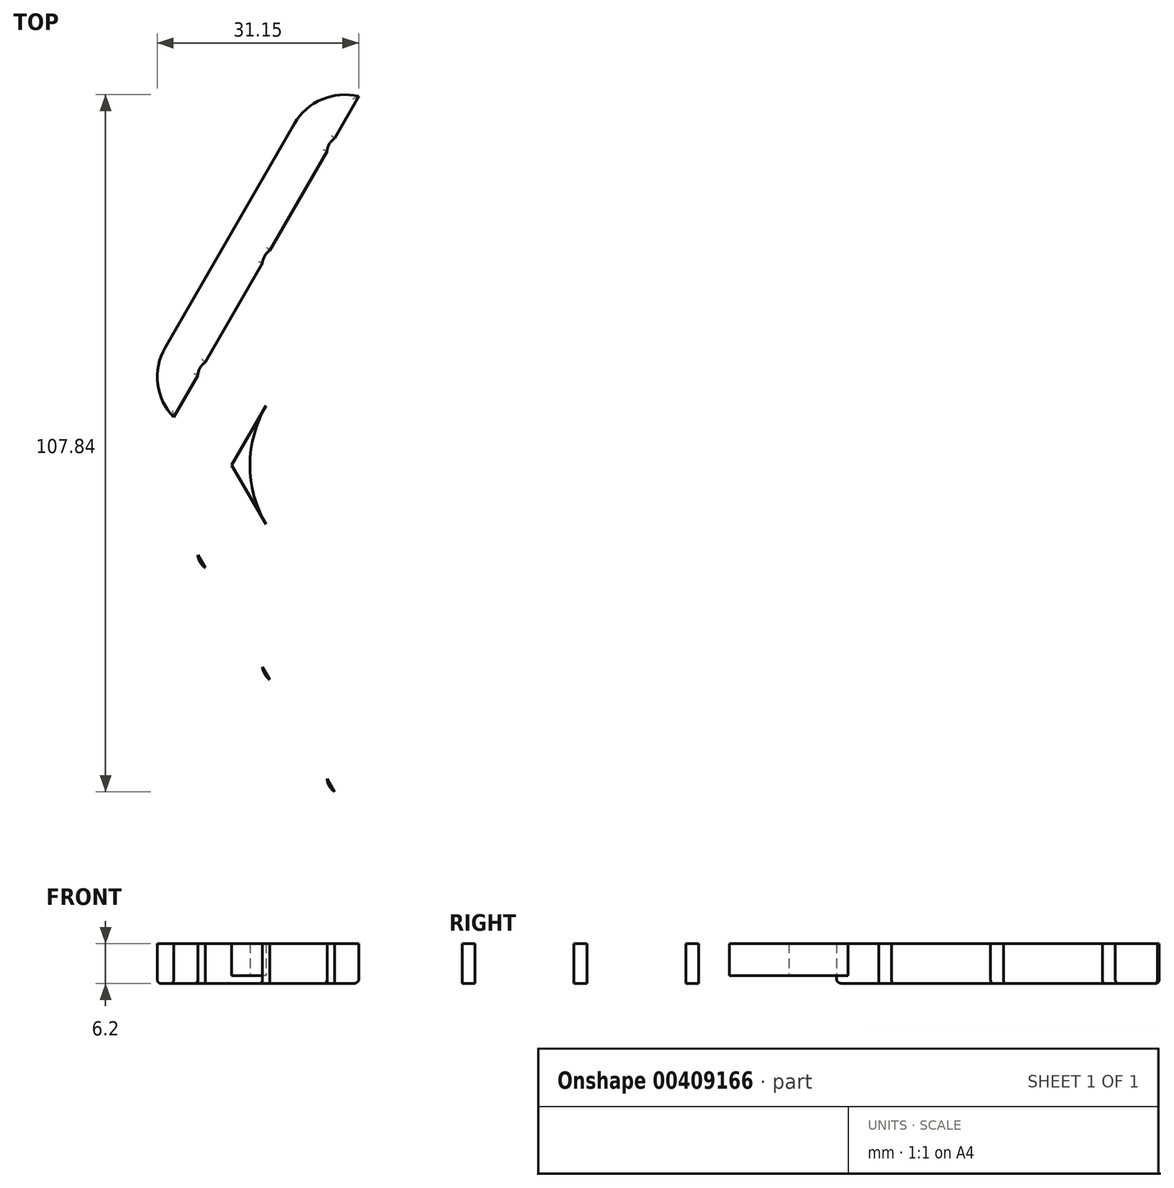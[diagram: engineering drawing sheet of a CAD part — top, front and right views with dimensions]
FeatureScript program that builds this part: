
annotation { "Feature Type Name" : "Feature", "Feature Type Description" : "" }
export const myFeature = defineFeature(function(context is Context, id is Id, definition is map)
    precondition{}
    {
        {
            var Q0;
            Q0=qCreatedBy(makeId("Top.planeOp"),FACE);
            var sketch = newSketch(context, id + "F0", { "sketchPlane" : qUnion([Q0])});
            skLineSegment(sketch, "E0", {"start": v(0, 0) * mm, "end": v(40.15, 69.55) * mm, "construction": true});
            skLineSegment(sketch, "E1", {"start": v(40.15, -69.55) * mm, "end": v(0, 0) * mm, "construction": true});
            skLineSegment(sketch, "E2", {"start": v(-5.77, 10) * mm, "end": v(11.55, 0) * mm, "construction": true});
            skCircle(sketch, "E3", {"center": v(7.89, 13.66) * mm, "radius": 10 * mm, "construction": true});
            skCircle(sketch, "E4", {"center": v(7.89, 13.66) * mm, "radius": 2.75 * mm});
            skCircle(sketch, "E5", {"center": v(17.89, 30.98) * mm, "radius": 2.75 * mm});
            skCircle(sketch, "E6", {"center": v(27.89, 48.3) * mm, "radius": 2.75 * mm});
            skArc(sketch, "E7", {"start": v(0.1, 18.16) * mm, "mid": v(-0.07, 9.46) * mm, "end": v(7.2, 4.69) * mm});
            skArc(sketch, "E8", {"start": v(35.68, 43.8) * mm, "mid": v(32.39, 56.1) * mm, "end": v(20.1, 52.8) * mm});
            skLineSegment(sketch, "E9", {"start": v(0.1, 18.16) * mm, "end": v(20.1, 52.8) * mm});
            skCircle(sketch, "E10.MirrorC", {"center": v(7.89, -13.66) * mm, "radius": 2.75 * mm});
            skLineSegment(sketch, "E11.MirrorCS", {"start": v(-5.77, -10) * mm, "end": v(11.55, 0) * mm, "construction": true});
            skCircle(sketch, "E12.MirrorC", {"center": v(17.89, -30.98) * mm, "radius": 2.75 * mm});
            skCircle(sketch, "E13.MirrorC", {"center": v(27.89, -48.3) * mm, "radius": 2.75 * mm});
            skArc(sketch, "E14.MirrorCS", {"start": v(0.1, -18.16) * mm, "mid": v(-0.07, -9.46) * mm, "end": v(7.2, -4.69) * mm});
            skCircle(sketch, "E15.MirrorC", {"center": v(7.89, -13.66) * mm, "radius": 10 * mm, "construction": true});
            skArc(sketch, "E16.MirrorCS", {"start": v(35.68, -43.8) * mm, "mid": v(32.39, -56.1) * mm, "end": v(20.1, -52.8) * mm});
            skLineSegment(sketch, "E17.MirrorCS", {"start": v(0.1, -18.16) * mm, "end": v(20.1, -52.8) * mm});
            skArc(sketch, "E18", {"start": v(7.2, 4.69) * mm, "mid": v(11.55, 0) * mm, "end": v(7.2, -4.69) * mm, "construction": true});
            skCircle(sketch, "E19", {"center": v(17.89, 30.98) * mm, "radius": 2.5 * mm, "construction": true});
            skLineSegment(sketch, "E20", {"start": v(34.37, 54.54) * mm, "end": v(5.73, 4.92) * mm});
            skLineSegment(sketch, "E21.MirrorCS", {"start": v(30.04, 57.04) * mm, "end": v(1.4, 7.42) * mm});
            skLineSegment(sketch, "E22.MirrorCS", {"start": v(30.04, -57.04) * mm, "end": v(1.4, -7.42) * mm});
            skLineSegment(sketch, "E23.MirrorCS", {"start": v(34.37, -54.54) * mm, "end": v(5.73, -4.92) * mm});
            skArc(sketch, "E24", {"start": v(0.1, 18.16) * mm, "mid": v(-4.77, 0) * mm, "end": v(0.1, -18.16) * mm});
            skCircle(sketch, "E25", {"center": v(0, 0) * mm, "radius": 2.75 * mm, "construction": true});
            skLineSegment(sketch, "E26", {"start": v(11.55, 0) * mm, "end": v(-4.77, 0) * mm, "construction": true});
            skLineSegment(sketch, "E27", {"start": v(11.15, 0) * mm, "end": v(-3.74, -8.6) * mm, "construction": true});
            skLineSegment(sketch, "E28.MirrorCS", {"start": v(11.15, 0) * mm, "end": v(-3.74, 8.6) * mm, "construction": true});
            skLineSegment(sketch, "E29", {"start": v(35.68, 43.8) * mm, "end": v(10.4, 0) * mm});
            skLineSegment(sketch, "E30.MirrorCS", {"start": v(35.68, -43.8) * mm, "end": v(10.4, 0) * mm});
            skArc(sketch, "E31", {"start": v(15.68, 9.16) * mm, "mid": v(13.23, 0) * mm, "end": v(15.68, -9.16) * mm});
            skSolve(sketch);
        }
        {
            var Q0;
            {var subQ4=sQuery(id+"F0.wireOp",EDGE,"E18");Q0=makeQuery(id+"F0.imprint","IMPRINT",FACE,{"disambiguationData":[TD([[makeQuery(id+"F0.imprint","IMPRINT",EDGE,{"derivedFrom":subQ4}),1.0]])]});}
            var Q1;
            {var subQ0=sQuery(id+"F0.wireOp",EDGE,"E9");Q1=makeQuery(id+"F0.imprint","IMPRINT",FACE,{"disambiguationData":[TD([[makeQuery(id+"F0.imprint","IMPRINT",EDGE,{"derivedFrom":subQ0}),-1.0]])]});}
            var Q2;
            {var subQ0=sQuery(id+"F0.wireOp",EDGE,"E21.MirrorCS");var subQ1=sQuery(id+"F0.wireOp",EDGE,"E5");var subQ2=makeQuery(id+"F0.imprint","INTERSECT",VERTEX,{"disambiguationData":[OD(1.0)],"derivedFrom":[subQ1,subQ0]});Q2=makeQuery(id+"F0.imprint","IMPRINT",FACE,{"disambiguationData":[TD([[makeQuery(id+"F0.imprint","IMPRINT",EDGE,{"disambiguationData":[TD([[subQ2,1.0]])],"derivedFrom":subQ1}),-1.0]])]});}
            var Q3;
            {var subQ0=sQuery(id+"F0.wireOp",EDGE,"E21.MirrorCS");var subQ1=sQuery(id+"F0.wireOp",EDGE,"E6");var subQ2=makeQuery(id+"F0.imprint","INTERSECT",VERTEX,{"disambiguationData":[OD(1.0)],"derivedFrom":[subQ1,subQ0]});Q3=makeQuery(id+"F0.imprint","IMPRINT",FACE,{"disambiguationData":[TD([[makeQuery(id+"F0.imprint","IMPRINT",EDGE,{"disambiguationData":[TD([[subQ2,1.0]])],"derivedFrom":subQ1}),-1.0]])]});}
            var Q4;
            {var subQ0=sQuery(id+"F0.wireOp",EDGE,"E21.MirrorCS");var subQ1=sQuery(id+"F0.wireOp",EDGE,"E4");var subQ2=makeQuery(id+"F0.imprint","INTERSECT",VERTEX,{"disambiguationData":[OD(1.0)],"derivedFrom":[subQ1,subQ0]});Q4=makeQuery(id+"F0.imprint","IMPRINT",FACE,{"disambiguationData":[TD([[makeQuery(id+"F0.imprint","IMPRINT",EDGE,{"disambiguationData":[TD([[subQ2,1.0]])],"derivedFrom":subQ1}),-1.0]])]});}
            var Q5;
            {var subQ0=sQuery(id+"F0.wireOp",EDGE,"E21.MirrorCS");var subQ1=sQuery(id+"F0.wireOp",EDGE,"E4");var subQ2=makeQuery(id+"F0.imprint","INTERSECT",VERTEX,{"disambiguationData":[OD(0.0)],"derivedFrom":[subQ1,subQ0]});Q5=makeQuery(id+"F0.imprint","IMPRINT",FACE,{"disambiguationData":[TD([[makeQuery(id+"F0.imprint","IMPRINT",EDGE,{"disambiguationData":[TD([[subQ2,-1.0]])],"derivedFrom":subQ1}),-1.0]])]});}
            var Q6;
            {var subQ0=sQuery(id+"F0.wireOp",EDGE,"E22.MirrorCS");var subQ1=sQuery(id+"F0.wireOp",EDGE,"E10.MirrorC");var subQ2=makeQuery(id+"F0.imprint","INTERSECT",VERTEX,{"disambiguationData":[OD(0.0)],"derivedFrom":[subQ1,subQ0]});Q6=makeQuery(id+"F0.imprint","IMPRINT",FACE,{"disambiguationData":[TD([[makeQuery(id+"F0.imprint","IMPRINT",EDGE,{"disambiguationData":[TD([[subQ2,-1.0]])],"derivedFrom":subQ1}),1.0]])]});}
            var Q7;
            {var subQ0=sQuery(id+"F0.wireOp",EDGE,"E22.MirrorCS");var subQ1=sQuery(id+"F0.wireOp",EDGE,"E10.MirrorC");var subQ2=makeQuery(id+"F0.imprint","INTERSECT",VERTEX,{"disambiguationData":[OD(1.0)],"derivedFrom":[subQ1,subQ0]});Q7=makeQuery(id+"F0.imprint","IMPRINT",FACE,{"disambiguationData":[TD([[makeQuery(id+"F0.imprint","IMPRINT",EDGE,{"disambiguationData":[TD([[subQ2,1.0]])],"derivedFrom":subQ1}),1.0]])]});}
            var Q8;
            {var subQ0=sQuery(id+"F0.wireOp",EDGE,"E22.MirrorCS");var subQ1=sQuery(id+"F0.wireOp",EDGE,"E12.MirrorC");var subQ2=makeQuery(id+"F0.imprint","INTERSECT",VERTEX,{"disambiguationData":[OD(1.0)],"derivedFrom":[subQ1,subQ0]});Q8=makeQuery(id+"F0.imprint","IMPRINT",FACE,{"disambiguationData":[TD([[makeQuery(id+"F0.imprint","IMPRINT",EDGE,{"disambiguationData":[TD([[subQ2,1.0]])],"derivedFrom":subQ1}),1.0]])]});}
            var Q9;
            {var subQ0=sQuery(id+"F0.wireOp",EDGE,"E22.MirrorCS");var subQ1=sQuery(id+"F0.wireOp",EDGE,"E13.MirrorC");var subQ2=makeQuery(id+"F0.imprint","INTERSECT",VERTEX,{"disambiguationData":[OD(1.0)],"derivedFrom":[subQ1,subQ0]});Q9=makeQuery(id+"F0.imprint","IMPRINT",FACE,{"disambiguationData":[TD([[makeQuery(id+"F0.imprint","IMPRINT",EDGE,{"disambiguationData":[TD([[subQ2,1.0]])],"derivedFrom":subQ1}),1.0]])]});}
            var Q10;
            {var subQ0=sQuery(id+"F0.wireOp",EDGE,"E17.MirrorCS");Q10=makeQuery(id+"F0.imprint","IMPRINT",FACE,{"disambiguationData":[TD([[makeQuery(id+"F0.imprint","IMPRINT",EDGE,{"derivedFrom":subQ0}),1.0]])]});}
            var Q11;
            {var subQ3=sQuery(id+"F0.wireOp",EDGE,"E18");Q11=makeQuery(id+"F0.imprint","IMPRINT",FACE,{"disambiguationData":[TD([[makeQuery(id+"F0.imprint","IMPRINT",EDGE,{"derivedFrom":subQ3}),-1.0]])]});}
            var Q12;
            {var subQ1=sQuery(id+"F0.wireOp",EDGE,"E2");var subQ3=sQuery(id+"F0.wireOp",EDGE,"E24");var subQ4=makeQuery(id+"F0.imprint","INTERSECT",VERTEX,{"derivedFrom":[subQ1,subQ3]});Q12=makeQuery(id+"F0.imprint","IMPRINT",FACE,{"disambiguationData":[TD([[makeQuery(id+"F0.imprint","IMPRINT",EDGE,{"disambiguationData":[TD([[subQ4,-1.0]])],"derivedFrom":subQ3}),1.0]])]});}
            var Q13;
            {var subQ3=sQuery(id+"F0.wireOp",EDGE,"E31");Q13=makeQuery(id+"F0.imprint","IMPRINT",FACE,{"disambiguationData":[TD([[makeQuery(id+"F0.imprint","IMPRINT",EDGE,{"derivedFrom":subQ3}),-1.0]])]});}
            extrude(context, id + "F1", {"entities" : qUnion([Q0, Q1, Q2, Q3, Q4, Q5, Q6, Q7, Q8, Q9, Q10, Q11, Q12, Q13]), "depth" : 5 * mm, "offsetDistance" : 25 * mm});
        }
        {
            var Q0;
            {var subQ0=sQuery(id+"F0.wireOp",EDGE,"E22.MirrorCS");var subQ1=sQuery(id+"F0.wireOp",EDGE,"E13.MirrorC");var subQ2=makeQuery(id+"F0.imprint","INTERSECT",VERTEX,{"disambiguationData":[OD(1.0)],"derivedFrom":[subQ1,subQ0]});Q0=makeQuery(id+"F0.imprint","IMPRINT",FACE,{"disambiguationData":[TD([[makeQuery(id+"F0.imprint","IMPRINT",EDGE,{"disambiguationData":[TD([[subQ2,1.0]])],"derivedFrom":subQ1}),1.0]])]});}
            var Q1;
            {var subQ0=sQuery(id+"F0.wireOp",EDGE,"E22.MirrorCS");var subQ1=sQuery(id+"F0.wireOp",EDGE,"E12.MirrorC");var subQ2=makeQuery(id+"F0.imprint","INTERSECT",VERTEX,{"disambiguationData":[OD(1.0)],"derivedFrom":[subQ1,subQ0]});Q1=makeQuery(id+"F0.imprint","IMPRINT",FACE,{"disambiguationData":[TD([[makeQuery(id+"F0.imprint","IMPRINT",EDGE,{"disambiguationData":[TD([[subQ2,1.0]])],"derivedFrom":subQ1}),1.0]])]});}
            var Q2;
            {var subQ0=sQuery(id+"F0.wireOp",EDGE,"E22.MirrorCS");var subQ1=sQuery(id+"F0.wireOp",EDGE,"E10.MirrorC");var subQ2=makeQuery(id+"F0.imprint","INTERSECT",VERTEX,{"disambiguationData":[OD(1.0)],"derivedFrom":[subQ1,subQ0]});Q2=makeQuery(id+"F0.imprint","IMPRINT",FACE,{"disambiguationData":[TD([[makeQuery(id+"F0.imprint","IMPRINT",EDGE,{"disambiguationData":[TD([[subQ2,1.0]])],"derivedFrom":subQ1}),1.0]])]});}
            var Q3;
            {var subQ0=sQuery(id+"F0.wireOp",EDGE,"E21.MirrorCS");var subQ1=sQuery(id+"F0.wireOp",EDGE,"E4");var subQ2=makeQuery(id+"F0.imprint","INTERSECT",VERTEX,{"disambiguationData":[OD(1.0)],"derivedFrom":[subQ1,subQ0]});Q3=makeQuery(id+"F0.imprint","IMPRINT",FACE,{"disambiguationData":[TD([[makeQuery(id+"F0.imprint","IMPRINT",EDGE,{"disambiguationData":[TD([[subQ2,1.0]])],"derivedFrom":subQ1}),-1.0]])]});}
            var Q4;
            {var subQ0=sQuery(id+"F0.wireOp",EDGE,"E21.MirrorCS");var subQ1=sQuery(id+"F0.wireOp",EDGE,"E5");var subQ2=makeQuery(id+"F0.imprint","INTERSECT",VERTEX,{"disambiguationData":[OD(1.0)],"derivedFrom":[subQ1,subQ0]});Q4=makeQuery(id+"F0.imprint","IMPRINT",FACE,{"disambiguationData":[TD([[makeQuery(id+"F0.imprint","IMPRINT",EDGE,{"disambiguationData":[TD([[subQ2,1.0]])],"derivedFrom":subQ1}),-1.0]])]});}
            var Q5;
            {var subQ0=sQuery(id+"F0.wireOp",EDGE,"E21.MirrorCS");var subQ1=sQuery(id+"F0.wireOp",EDGE,"E6");var subQ2=makeQuery(id+"F0.imprint","INTERSECT",VERTEX,{"disambiguationData":[OD(1.0)],"derivedFrom":[subQ1,subQ0]});Q5=makeQuery(id+"F0.imprint","IMPRINT",FACE,{"disambiguationData":[TD([[makeQuery(id+"F0.imprint","IMPRINT",EDGE,{"disambiguationData":[TD([[subQ2,1.0]])],"derivedFrom":subQ1}),-1.0]])]});}
            extrude(context, id + "F2", {"entities" : qUnion([Q0, Q1, Q2, Q3, Q4, Q5]), "operationType" : NewBodyOperationType.ADD, "oppositeDirection" : true, "depth" : 1.2 * mm, "offsetDistance" : 25 * mm});
        }
        {
            var Q0;
            Q0=makeQuery(id+"F2.opExtrude","CAP_FACE",FACE,{"disambiguationData":[OSD([sQuery(id+"F0.wireOp",EDGE,"E5"),sQuery(id+"F0.wireOp",EDGE,"E6"),sQuery(id+"F0.wireOp",EDGE,"E20"),sQuery(id+"F0.wireOp",EDGE,"E21.MirrorCS")])],"isStart":false});
            var Q1;
            Q1=makeQuery(id+"F2.opExtrude","CAP_FACE",FACE,{"disambiguationData":[OSD([sQuery(id+"F0.wireOp",EDGE,"E6"),sQuery(id+"F0.wireOp",EDGE,"E8"),sQuery(id+"F0.wireOp",EDGE,"E20"),sQuery(id+"F0.wireOp",EDGE,"E21.MirrorCS")])],"isStart":false});
            var Q2;
            Q2=makeQuery(id+"F2.opExtrude","CAP_FACE",FACE,{"disambiguationData":[OSD([sQuery(id+"F0.wireOp",EDGE,"E4"),sQuery(id+"F0.wireOp",EDGE,"E5"),sQuery(id+"F0.wireOp",EDGE,"E20"),sQuery(id+"F0.wireOp",EDGE,"E21.MirrorCS")])],"isStart":false});
            var Q3;
            Q3=makeQuery(id+"F2.opExtrude","CAP_FACE",FACE,{"disambiguationData":[OSD([sQuery(id+"F0.wireOp",EDGE,"E4"),sQuery(id+"F0.wireOp",EDGE,"E7"),sQuery(id+"F0.wireOp",EDGE,"E20"),sQuery(id+"F0.wireOp",EDGE,"E21.MirrorCS")])],"isStart":false});
            var Q4;
            Q4=makeQuery(id+"F2.opExtrude","CAP_FACE",FACE,{"disambiguationData":[OSD([sQuery(id+"F0.wireOp",EDGE,"E10.MirrorC"),sQuery(id+"F0.wireOp",EDGE,"E14.MirrorCS"),sQuery(id+"F0.wireOp",EDGE,"E22.MirrorCS"),sQuery(id+"F0.wireOp",EDGE,"E23.MirrorCS")])],"isStart":false});
            var Q5;
            Q5=makeQuery(id+"F2.opExtrude","CAP_FACE",FACE,{"disambiguationData":[OSD([sQuery(id+"F0.wireOp",EDGE,"E10.MirrorC"),sQuery(id+"F0.wireOp",EDGE,"E12.MirrorC"),sQuery(id+"F0.wireOp",EDGE,"E22.MirrorCS"),sQuery(id+"F0.wireOp",EDGE,"E23.MirrorCS")])],"isStart":false});
            var Q6;
            Q6=makeQuery(id+"F2.opExtrude","CAP_FACE",FACE,{"disambiguationData":[OSD([sQuery(id+"F0.wireOp",EDGE,"E13.MirrorC"),sQuery(id+"F0.wireOp",EDGE,"E16.MirrorCS"),sQuery(id+"F0.wireOp",EDGE,"E22.MirrorCS"),sQuery(id+"F0.wireOp",EDGE,"E23.MirrorCS")])],"isStart":false});
            var Q7;
            Q7=makeQuery(id+"F2.opExtrude","CAP_FACE",FACE,{"disambiguationData":[OSD([sQuery(id+"F0.wireOp",EDGE,"E12.MirrorC"),sQuery(id+"F0.wireOp",EDGE,"E13.MirrorC"),sQuery(id+"F0.wireOp",EDGE,"E22.MirrorCS"),sQuery(id+"F0.wireOp",EDGE,"E23.MirrorCS")])],"isStart":false});
            var Q8;
            Q8=makeQuery(id+"F2.opExtrude","CAP_FACE",FACE,{"disambiguationData":[OSD([sQuery(id+"F0.wireOp",EDGE,"E2"),sQuery(id+"F0.wireOp",EDGE,"AwdjGCNM-xevV-rkCu-k57T-VdCHvtGFgJDu"),sQuery(id+"F0.wireOp",EDGE,"E24")])],"isStart":false});
            fillet(context, id + "F3", {"entities" : qUnion([Q0, Q1, Q2, Q3, Q4, Q5, Q6, Q7, Q8]), "radius" : 0.6 * mm, "tangentPropagation" : true, "allowEdgeOverflow" : false});
        }
    });
